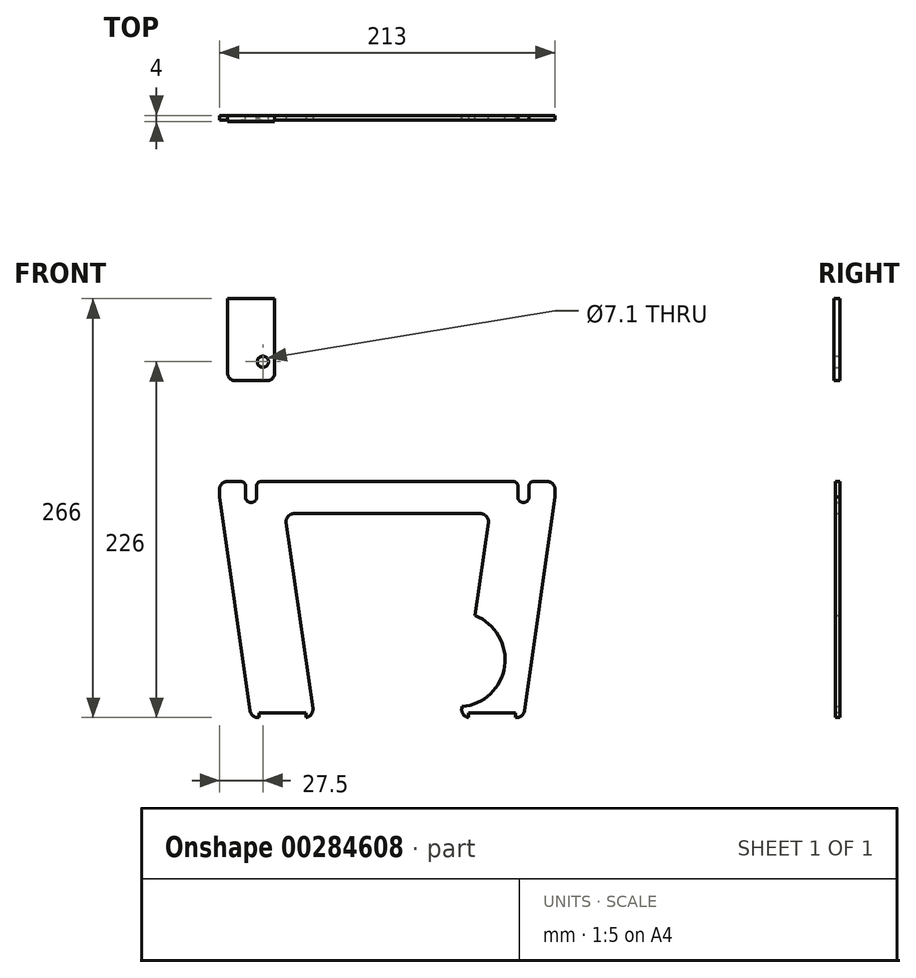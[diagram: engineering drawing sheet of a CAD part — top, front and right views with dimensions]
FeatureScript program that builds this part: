
annotation { "Feature Type Name" : "Feature", "Feature Type Description" : "" }
export const myFeature = defineFeature(function(context is Context, id is Id, definition is map)
    precondition{}
    {
        {
            var Q0;
            Q0=qCreatedBy(makeId("Front.planeOp"),FACE);
            var sketch = newSketch(context, id + "F0", { "sketchPlane" : qUnion([Q0])});
            skLineSegment(sketch, "E0", {"start": v(0, 0) * mm, "end": v(173, 0) * mm, "construction": true});
            skLineSegment(sketch, "E1", {"start": v(0, 0) * mm, "end": v(-20, 0) * mm, "construction": true});
            skLineSegment(sketch, "E2", {"start": v(27.5, 0) * mm, "end": v(27.5, -140) * mm, "construction": true});
            skLineSegment(sketch, "E3", {"start": v(173, 0) * mm, "end": v(193, 0) * mm, "construction": true});
            skLineSegment(sketch, "E4", {"start": v(145.5, 0) * mm, "end": v(145.5, -140) * mm, "construction": true});
            skLineSegment(sketch, "E5", {"start": v(-20, 0) * mm, "end": v(0, -140) * mm});
            skLineSegment(sketch, "E6", {"start": v(193, 0) * mm, "end": v(173, -140) * mm});
            skLineSegment(sketch, "E7", {"start": v(0, -140) * mm, "end": v(40, -140) * mm});
            skLineSegment(sketch, "E8", {"start": v(173, -140) * mm, "end": v(133, -140) * mm});
            skPoint(sketch, "E9", {"position": v(20, 0) * mm});
            skLineSegment(sketch, "E10", {"start": v(40, -140) * mm, "end": v(21.5, -10.5) * mm});
            skArc(sketch, "E11", {"start": v(-3.5, 0) * mm, "mid": v(0, -3.5) * mm, "end": v(3.5, 0) * mm});
            skPoint(sketch, "E12", {"position": v(153, 0) * mm});
            skLineSegment(sketch, "E13", {"start": v(133, -140) * mm, "end": v(151.5, -10.5) * mm});
            skArc(sketch, "E14", {"start": v(169.5, 0) * mm, "mid": v(173, -3.5) * mm, "end": v(176.5, 0) * mm});
            skLineSegment(sketch, "E15", {"start": v(21.5, -10.5) * mm, "end": v(151.5, -10.5) * mm});
            skLineSegment(sketch, "E16", {"start": v(-20, 0) * mm, "end": v(-20, 10) * mm});
            skLineSegment(sketch, "E17", {"start": v(-20, 10) * mm, "end": v(-3.5, 10) * mm});
            skLineSegment(sketch, "E18", {"start": v(-3.5, 10) * mm, "end": v(-3.5, 0) * mm});
            skLineSegment(sketch, "E19", {"start": v(3.5, 0) * mm, "end": v(3.5, 10) * mm});
            skLineSegment(sketch, "E20", {"start": v(3.5, 10) * mm, "end": v(20, 10) * mm});
            skLineSegment(sketch, "E21", {"start": v(153, 10) * mm, "end": v(169.5, 10) * mm});
            skLineSegment(sketch, "E22", {"start": v(169.5, 10) * mm, "end": v(169.5, 0) * mm});
            skLineSegment(sketch, "E23", {"start": v(176.5, 0) * mm, "end": v(176.5, 10) * mm});
            skLineSegment(sketch, "E24", {"start": v(176.5, 10) * mm, "end": v(193, 10) * mm});
            skLineSegment(sketch, "E25", {"start": v(193, 10) * mm, "end": v(193, 0) * mm});
            skLineSegment(sketch, "E26", {"start": v(20, 10) * mm, "end": v(153, 10) * mm});
            skPoint(sketch, "E27", {"position": v(133.99, -133.07) * mm});
            skArc(sketch, "E28", {"start": v(133.99, -133.07) * mm, "mid": v(161.02, -107.43) * mm, "end": v(142.25, -75.25) * mm});
            skSolve(sketch);
        }
        {
            var Q0;
            Q0=makeQuery(id+"F0.imprint","IMPRINT",FACE,{"disambiguationData":[TD([[makeQuery(id+"F0.imprint","IMPRINT",EDGE,{"derivedFrom":sQuery(id+"F0.wireOp",EDGE,"E5")}),1.0]])]});
            extrude(context, id + "F1", {"entities" : qUnion([Q0]), "depth" : 3 * mm});
        }
        {
            var Q0;
            Q0=makeQuery(id+"F1.opExtrude","CAP_FACE",FACE,{"disambiguationData":[OSD([sQuery(id+"F0.wireOp",EDGE,"E5"),sQuery(id+"F0.wireOp",EDGE,"E6"),sQuery(id+"F0.wireOp",EDGE,"E7"),sQuery(id+"F0.wireOp",EDGE,"E8"),sQuery(id+"F0.wireOp",EDGE,"E10"),sQuery(id+"F0.wireOp",EDGE,"E11"),sQuery(id+"F0.wireOp",EDGE,"E13"),sQuery(id+"F0.wireOp",EDGE,"E14"),sQuery(id+"F0.wireOp",EDGE,"E15"),sQuery(id+"F0.wireOp",EDGE,"E16"),sQuery(id+"F0.wireOp",EDGE,"E17"),sQuery(id+"F0.wireOp",EDGE,"E18"),sQuery(id+"F0.wireOp",EDGE,"E19"),sQuery(id+"F0.wireOp",EDGE,"E20"),sQuery(id+"F0.wireOp",EDGE,"E21"),sQuery(id+"F0.wireOp",EDGE,"E22"),sQuery(id+"F0.wireOp",EDGE,"E23"),sQuery(id+"F0.wireOp",EDGE,"E24"),sQuery(id+"F0.wireOp",EDGE,"E25"),sQuery(id+"F0.wireOp",EDGE,"E26")])],"isStart":false});
            var sketch = newSketch(context, id + "F2", { "sketchPlane" : qUnion([Q0])});
            skLineSegment(sketch, "E29", {"start": v(0, -140) * mm, "end": v(5, -140) * mm, "construction": true});
            skLineSegment(sketch, "E30", {"start": v(5, -140) * mm, "end": v(5, -137) * mm});
            skLineSegment(sketch, "E31", {"start": v(5, -137) * mm, "end": v(35, -137) * mm});
            skLineSegment(sketch, "E32", {"start": v(35, -137) * mm, "end": v(35, -140) * mm});
            skLineSegment(sketch, "E33", {"start": v(5, -140) * mm, "end": v(35, -140) * mm});
            skLineSegment(sketch, "E34", {"start": v(173, -140) * mm, "end": v(168, -140) * mm, "construction": true});
            skLineSegment(sketch, "E35", {"start": v(168, -140) * mm, "end": v(168, -137) * mm});
            skLineSegment(sketch, "E36", {"start": v(168, -137) * mm, "end": v(138, -137) * mm});
            skLineSegment(sketch, "E37", {"start": v(138, -137) * mm, "end": v(138, -140) * mm});
            skLineSegment(sketch, "E38", {"start": v(138, -140) * mm, "end": v(168, -140) * mm});
            skSolve(sketch);
        }
        {
            var Q0;
            Q0=makeQuery(id+"F2.imprint","IMPRINT",FACE,{"disambiguationData":[TD([[makeQuery(id+"F2.imprint","IMPRINT",EDGE,{"derivedFrom":sQuery(id+"F2.wireOp",EDGE,"E30")}),-1.0]])]});
            var Q1;
            Q1=makeQuery(id+"F2.imprint","IMPRINT",FACE,{"disambiguationData":[TD([[makeQuery(id+"F2.imprint","IMPRINT",EDGE,{"derivedFrom":sQuery(id+"F2.wireOp",EDGE,"E35")}),1.0]])]});
            extrude(context, id + "F3", {"entities" : qUnion([Q0, Q1]), "operationType" : NewBodyOperationType.REMOVE, "oppositeDirection" : true, "depth" : 25 * mm});
        }
        {
            var Q0;
            Q0=qCreatedBy(makeId("Front.planeOp"),FACE);
            var sketch = newSketch(context, id + "F4", { "sketchPlane" : qUnion([Q0])});
            skLineSegment(sketch, "E39", {"start": v(0, 0) * mm, "end": v(0, 100) * mm, "construction": true});
            skLineSegment(sketch, "E40.bottom", {"start": v(15, 74) * mm, "end": v(-15, 74) * mm});
            skLineSegment(sketch, "E40.top", {"start": v(15, 126) * mm, "end": v(-15, 126) * mm});
            skLineSegment(sketch, "E40.left", {"start": v(15, 74) * mm, "end": v(15, 126) * mm});
            skLineSegment(sketch, "E40.right", {"start": v(-15, 74) * mm, "end": v(-15, 126) * mm});
            skPoint(sketch, "E40.middle", {"position": v(0, 100) * mm});
            skLineSegment(sketch, "E41", {"start": v(7.5, 74) * mm, "end": v(7.5, 86) * mm, "construction": true});
            skLineSegment(sketch, "E42", {"start": v(7.5, 86) * mm, "end": v(15, 86) * mm, "construction": true});
            skSolve(sketch);
        }
        {
            var Q0;
            Q0=qSketchRegion(id+"F4",true);
            extrude(context, id + "F5", {"entities" : qUnion([Q0]), "depth" : 4 * mm});
        }
        {
            var Q0;
            Q0=sQuery(id+"F4.wireOp",VERTEX,"E42.start");
            var Q1;
            Q1=makeQuery(id+"F5.opExtrude","SWEPT_BODY",BODY,{"disambiguationData":[OSD([sQuery(id+"F4.wireOp",EDGE,"E40.bottom"),sQuery(id+"F4.wireOp",EDGE,"E40.top"),sQuery(id+"F4.wireOp",EDGE,"E40.left"),sQuery(id+"F4.wireOp",EDGE,"E40.right")])]});
            hole(context, id + "F6", {"style" : HoleStyle.SIMPLE, "endStyle" : HoleEndStyle.THROUGH, "oppositeDirection" : true, "holeDiameter" : 7.1 * mm, "locations" : qUnion([Q0]), "scope" : qUnion([Q1]), "isTappedThrough" : true});
        }
        {
            var Q0;
            Q0=makeQuery(id+"F1.opExtrude","SWEPT_EDGE",EDGE,{"disambiguationData":[OSD([sQuery(id+"F0.wireOp",EDGE,"E16"),sQuery(id+"F0.wireOp",EDGE,"E17")])]});
            var Q1;
            Q1=makeQuery(id+"F1.opExtrude","SWEPT_EDGE",EDGE,{"disambiguationData":[OSD([sQuery(id+"F0.wireOp",EDGE,"E5"),sQuery(id+"F0.wireOp",EDGE,"E7")])]});
            var Q2;
            Q2=makeQuery(id+"F1.opExtrude","SWEPT_EDGE",EDGE,{"disambiguationData":[OSD([sQuery(id+"F0.wireOp",EDGE,"E7"),sQuery(id+"F0.wireOp",EDGE,"E10")])]});
            var Q3;
            Q3=makeQuery(id+"F1.opExtrude","SWEPT_EDGE",EDGE,{"disambiguationData":[OSD([sQuery(id+"F0.wireOp",EDGE,"E8"),sQuery(id+"F0.wireOp",EDGE,"E13")])]});
            var Q4;
            Q4=makeQuery(id+"F1.opExtrude","SWEPT_EDGE",EDGE,{"disambiguationData":[OSD([sQuery(id+"F0.wireOp",EDGE,"E6"),sQuery(id+"F0.wireOp",EDGE,"E8")])]});
            var Q5;
            Q5=makeQuery(id+"F1.opExtrude","SWEPT_EDGE",EDGE,{"disambiguationData":[OSD([sQuery(id+"F0.wireOp",EDGE,"E13"),sQuery(id+"F0.wireOp",EDGE,"E15")])]});
            var Q6;
            Q6=makeQuery(id+"F1.opExtrude","SWEPT_EDGE",EDGE,{"disambiguationData":[OSD([sQuery(id+"F0.wireOp",EDGE,"E10"),sQuery(id+"F0.wireOp",EDGE,"E15")])]});
            var Q7;
            Q7=makeQuery(id+"F1.opExtrude","SWEPT_EDGE",EDGE,{"disambiguationData":[OSD([sQuery(id+"F0.wireOp",EDGE,"E24"),sQuery(id+"F0.wireOp",EDGE,"E25")])]});
            fillet(context, id + "F7", {"entities" : qUnion([Q0, Q1, Q2, Q3, Q4, Q5, Q6, Q7]), "radius" : 5 * mm, "tangentPropagation" : true, "allowEdgeOverflow" : false});
        }
        {
            var Q0;
            Q0=makeQuery(id+"F1.opExtrude","SWEPT_EDGE",EDGE,{"disambiguationData":[OSD([sQuery(id+"F0.wireOp",EDGE,"E21"),sQuery(id+"F0.wireOp",EDGE,"E22")])]});
            var Q1;
            Q1=makeQuery(id+"F1.opExtrude","SWEPT_EDGE",EDGE,{"disambiguationData":[OSD([sQuery(id+"F0.wireOp",EDGE,"E23"),sQuery(id+"F0.wireOp",EDGE,"E24")])]});
            var Q2;
            Q2=makeQuery(id+"F1.opExtrude","SWEPT_EDGE",EDGE,{"disambiguationData":[OSD([sQuery(id+"F0.wireOp",EDGE,"E17"),sQuery(id+"F0.wireOp",EDGE,"E18")])]});
            var Q3;
            Q3=makeQuery(id+"F1.opExtrude","SWEPT_EDGE",EDGE,{"disambiguationData":[OSD([sQuery(id+"F0.wireOp",EDGE,"E19"),sQuery(id+"F0.wireOp",EDGE,"E20")])]});
            fillet(context, id + "F8", {"entities" : qUnion([Q0, Q1, Q2, Q3]), "radius" : 3 * mm, "tangentPropagation" : true, "allowEdgeOverflow" : false});
        }
        {
            var Q0;
            Q0=makeQuery(id+"F5.opExtrude","SWEPT_EDGE",EDGE,{"disambiguationData":[OSD([sQuery(id+"F4.wireOp",EDGE,"E40.bottom"),sQuery(id+"F4.wireOp",EDGE,"E40.right")])]});
            var Q1;
            Q1=makeQuery(id+"F5.opExtrude","SWEPT_EDGE",EDGE,{"disambiguationData":[OSD([sQuery(id+"F4.wireOp",EDGE,"E40.bottom"),sQuery(id+"F4.wireOp",EDGE,"E40.left")])]});
            fillet(context, id + "F9", {"entities" : qUnion([Q0, Q1]), "radius" : 5 * mm, "tangentPropagation" : true, "allowEdgeOverflow" : false});
        }
    });
